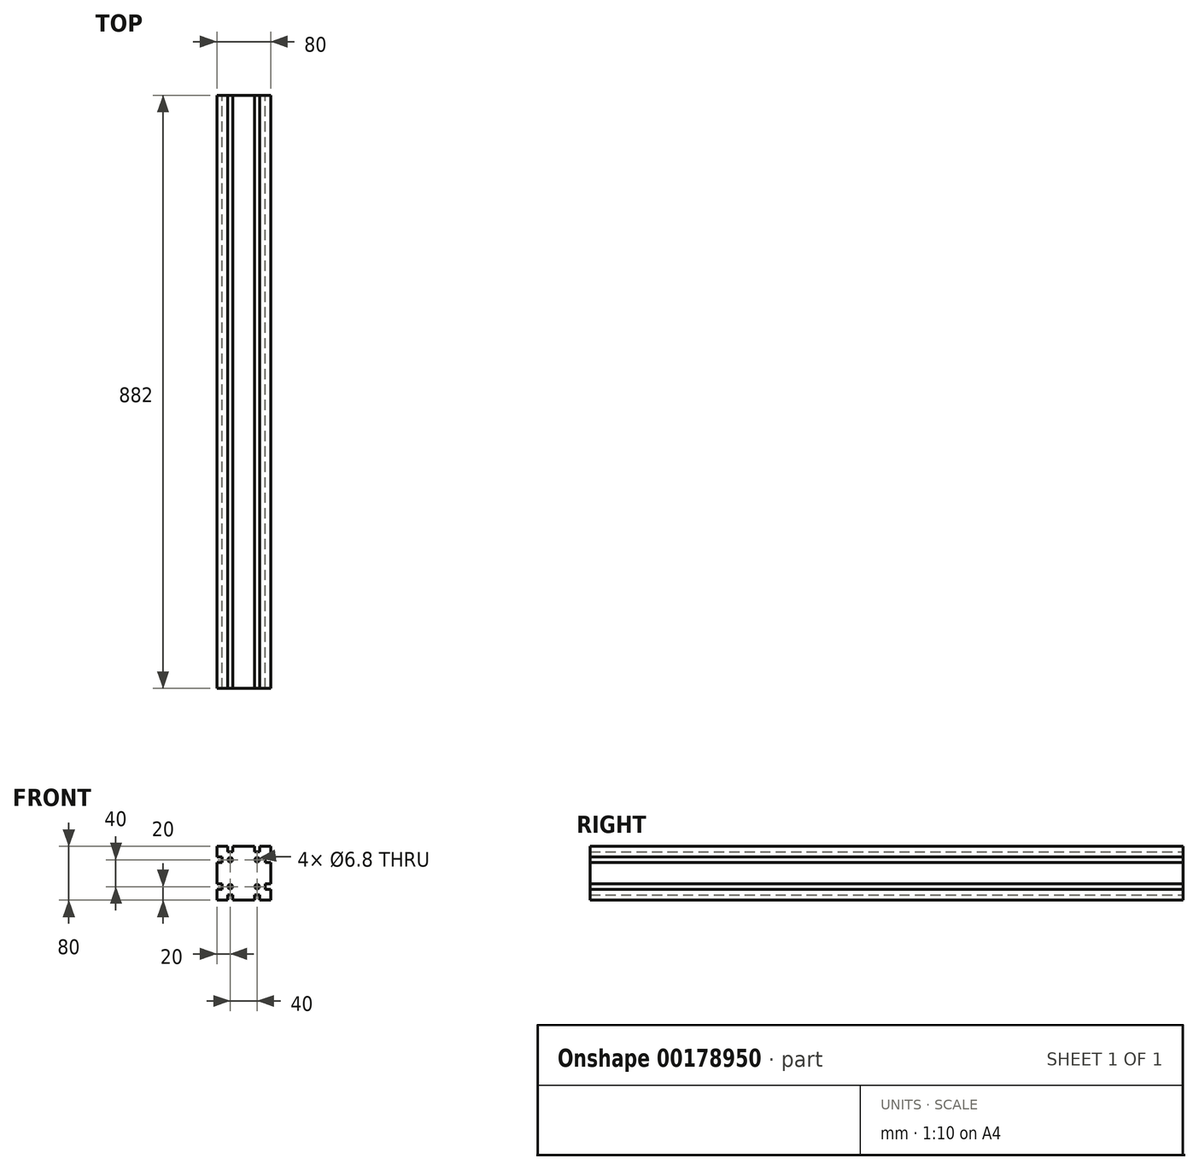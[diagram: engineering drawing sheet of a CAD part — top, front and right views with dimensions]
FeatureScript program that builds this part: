
annotation { "Feature Type Name" : "Feature", "Feature Type Description" : "" }
export const myFeature = defineFeature(function(context is Context, id is Id, definition is map)
    precondition{}
    {
        {
            var Q0;
            Q0=qCreatedBy(makeId("Front.planeOp"),FACE);
            var sketch = newSketch(context, id + "F0", { "sketchPlane" : qUnion([Q0])});
            skLineSegment(sketch, "E0.bottom", {"start": v(40, 40) * mm, "end": v(24, 40) * mm});
            skLineSegment(sketch, "E0.top", {"start": v(40, -40) * mm, "end": v(24, -40) * mm});
            skLineSegment(sketch, "E0.left", {"start": v(40, 40) * mm, "end": v(40, 24) * mm});
            skLineSegment(sketch, "E0.right", {"start": v(-40, 40) * mm, "end": v(-40, 24) * mm});
            skPoint(sketch, "E0.middle", {"position": v(0, 0) * mm});
            skLineSegment(sketch, "E1", {"start": v(-20, 40) * mm, "end": v(-20, 23.4) * mm});
            skLineSegment(sketch, "E2", {"start": v(20, 40) * mm, "end": v(20, 23.4) * mm});
            skCircle(sketch, "E3", {"center": v(-20, 20) * mm, "radius": 3.4 * mm});
            skCircle(sketch, "E4", {"center": v(20, 20) * mm, "radius": 3.4 * mm});
            skCircle(sketch, "E5", {"center": v(-20, -20) * mm, "radius": 3.4 * mm});
            skCircle(sketch, "E6", {"center": v(20, -20) * mm, "radius": 3.4 * mm});
            skLineSegment(sketch, "E7.bottom", {"start": v(-32, 16) * mm, "end": v(-40, 16) * mm});
            skLineSegment(sketch, "E7.top", {"start": v(-32, 24) * mm, "end": v(-40, 24) * mm});
            skLineSegment(sketch, "E7.left", {"start": v(-32, 16) * mm, "end": v(-32, 24) * mm});
            skPoint(sketch, "E7.middle", {"position": v(-40, 20) * mm});
            skLineSegment(sketch, "E8.top", {"start": v(-16, 32) * mm, "end": v(-24, 32) * mm});
            skLineSegment(sketch, "E8.left", {"start": v(-16, 40) * mm, "end": v(-16, 32) * mm});
            skLineSegment(sketch, "E8.right", {"start": v(-24, 40) * mm, "end": v(-24, 32) * mm});
            skPoint(sketch, "E8.middle", {"position": v(-20, 40) * mm});
            skLineSegment(sketch, "E9.top", {"start": v(24, 32) * mm, "end": v(16, 32) * mm});
            skLineSegment(sketch, "E9.left", {"start": v(24, 40) * mm, "end": v(24, 32) * mm});
            skLineSegment(sketch, "E9.right", {"start": v(16, 40) * mm, "end": v(16, 32) * mm});
            skPoint(sketch, "E9.middle", {"position": v(20, 40) * mm});
            skLineSegment(sketch, "E10.bottom", {"start": v(40, 16) * mm, "end": v(32, 16) * mm});
            skLineSegment(sketch, "E10.top", {"start": v(40, 24) * mm, "end": v(32, 24) * mm});
            skLineSegment(sketch, "E10.right", {"start": v(32, 16) * mm, "end": v(32, 24) * mm});
            skPoint(sketch, "E10.middle", {"position": v(40, 20) * mm});
            skLineSegment(sketch, "E11.bottom", {"start": v(40, -24) * mm, "end": v(32, -24) * mm});
            skLineSegment(sketch, "E11.top", {"start": v(40, -16) * mm, "end": v(32, -16) * mm});
            skLineSegment(sketch, "E11.right", {"start": v(32, -24) * mm, "end": v(32, -16) * mm});
            skPoint(sketch, "E11.middle", {"position": v(40, -20) * mm});
            skLineSegment(sketch, "E12.top", {"start": v(24, -32) * mm, "end": v(16, -32) * mm});
            skLineSegment(sketch, "E12.left", {"start": v(24, -40) * mm, "end": v(24, -32) * mm});
            skLineSegment(sketch, "E12.right", {"start": v(16, -40) * mm, "end": v(16, -32) * mm});
            skPoint(sketch, "E12.middle", {"position": v(20, -40) * mm});
            skLineSegment(sketch, "E13.top", {"start": v(-16, -32) * mm, "end": v(-24, -32) * mm});
            skLineSegment(sketch, "E13.left", {"start": v(-16, -40) * mm, "end": v(-16, -32) * mm});
            skLineSegment(sketch, "E13.right", {"start": v(-24, -40) * mm, "end": v(-24, -32) * mm});
            skPoint(sketch, "E13.middle", {"position": v(-20, -40) * mm});
            skLineSegment(sketch, "E14.bottom", {"start": v(-40, -16) * mm, "end": v(-32, -16) * mm});
            skLineSegment(sketch, "E14.top", {"start": v(-40, -24) * mm, "end": v(-32, -24) * mm});
            skLineSegment(sketch, "E14.right", {"start": v(-32, -16) * mm, "end": v(-32, -24) * mm});
            skPoint(sketch, "E14.middle", {"position": v(-40, -20) * mm});
            skPoint(sketch, "E15.orphan", {"position": v(-24, 48) * mm});
            skPoint(sketch, "E16.orphan", {"position": v(-16, 48) * mm});
            skLineSegment(sketch, "E17.trimOffspring", {"start": v(-24, 40) * mm, "end": v(-40, 40) * mm});
            skPoint(sketch, "E7.right.end.orphan", {"position": v(-48, 24) * mm});
            skPoint(sketch, "E7.right.start.orphan", {"position": v(-48, 16) * mm});
            skLineSegment(sketch, "E18.trimOffspring", {"start": v(-40, 16) * mm, "end": v(-40, -16) * mm});
            skLineSegment(sketch, "E19.trimOffspring", {"start": v(16, 40) * mm, "end": v(-16, 40) * mm});
            skPoint(sketch, "E9.bottom.end.orphan", {"position": v(16, 48) * mm});
            skPoint(sketch, "E9.bottom.start.orphan", {"position": v(24, 48) * mm});
            skPoint(sketch, "E10.left.end.orphan", {"position": v(48, 24) * mm});
            skPoint(sketch, "E10.left.start.orphan", {"position": v(48, 16) * mm});
            skLineSegment(sketch, "E20.trimOffspring", {"start": v(40, 16) * mm, "end": v(40, -16) * mm});
            skLineSegment(sketch, "E21.trimOffspring", {"start": v(-40, -24) * mm, "end": v(-40, -40) * mm});
            skPoint(sketch, "E14.left.start.orphan", {"position": v(-48, -16) * mm});
            skPoint(sketch, "E22.orphan", {"position": v(-48, -24) * mm});
            skLineSegment(sketch, "E23.trimOffspring", {"start": v(-24, -40) * mm, "end": v(-40, -40) * mm});
            skPoint(sketch, "E13.bottom.start.orphan", {"position": v(-16, -48) * mm});
            skPoint(sketch, "E24.orphan", {"position": v(-24, -48) * mm});
            skLineSegment(sketch, "E25.trimOffspring", {"start": v(16, -40) * mm, "end": v(-16, -40) * mm});
            skPoint(sketch, "E12.bottom.end.orphan", {"position": v(16, -48) * mm});
            skPoint(sketch, "E12.bottom.start.orphan", {"position": v(24, -48) * mm});
            skPoint(sketch, "E11.left.end.orphan", {"position": v(48, -16) * mm});
            skPoint(sketch, "E26.orphan", {"position": v(48, -24) * mm});
            skLineSegment(sketch, "E27.trimOffspring", {"start": v(40, -24) * mm, "end": v(40, -40) * mm});
            skSolve(sketch);
        }
        {
            var Q0;
            Q0=makeQuery(id+"F0.imprint","IMPRINT",FACE,{"disambiguationData":[TD([[makeQuery(id+"F0.imprint","IMPRINT",EDGE,{"derivedFrom":sQuery(id+"F0.wireOp",EDGE,"E0.bottom")}),1.0]])]});
            extrude(context, id + "F1", {"entities" : qUnion([Q0]), "depth" : 882 * mm});
        }
    });
